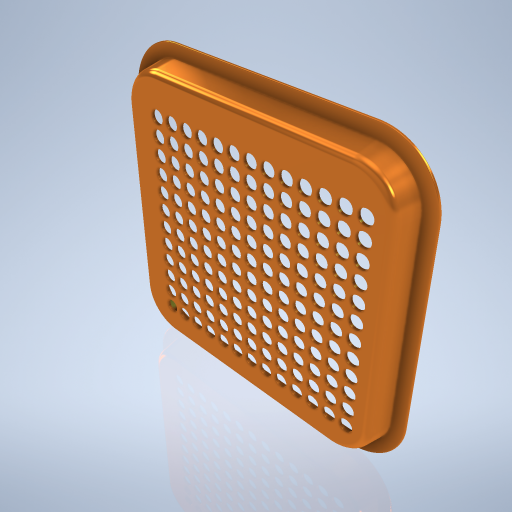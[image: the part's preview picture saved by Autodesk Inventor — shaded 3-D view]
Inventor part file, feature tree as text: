
AUTODESK INVENTOR PART (.ipt)
format: ipt  version: 2024.2 (Build 282272000, 272)  size: 988,672 bytes
history: native  units: mm
features: sketch x5, extrude x3, plane x2, mirror x2, fillet x2, pattern_linear x2, projected_geometry x2, revolve x1, other x1
ambient origin geometry x8: Origin, YZ Plane, XZ Plane, XY Plane, X Axis, Y Axis, Z Axis, Center Point
bodies: Body1 (feature_tree)
feature tree (20):
  extrude  "Extrusion4"  Depth=3.5mm
  revolve  "Umdrehung2"
  extrude  "Extrusion5"  Depth=3.5mm
  plane  "Arbeitsebene4"
  mirror  "Spiegeln4"
  plane  "Arbeitsebene5"
  mirror  "Spiegeln6"
  fillet  "Rundung1"  Radius=17.453293mm
  fillet  "Rundung2"  Radius=20.0mm
  extrude  "Extrusion6"  Depth=10.0mm
  pattern_linear  "Rechteckige Anordnung2"  Count1=12 Spacing1=0.0mm
  pattern_linear  "Rechteckige Anordnung3"  Count1=7  [1 undecoded]
  other  "Prägen1"
  sketch  "Skizze1"  dims[d0=195.0mm d1=3.5mm]
  sketch  "Skizze10"  dims[d2=3.5mm d3=3.5mm d4=17.453293mm d5=20.0mm]
  sketch  "Skizze11"  dims[d6=33.5mm d7=10.0mm d26=120.0mm d27=0.0mm d30=70.0mm]
  projected_geometry  "Projizierte Kontur5"
  sketch  "Skizze12"  dims[d31=90.0deg]
  projected_geometry  "Projizierte Kontur6"
  sketch  "Skizze13"  dims[d32=120.0mm d33=0.0mm d34=0.0mm d35=0.0mm d36=5.0mm d37=1.0mm d38=17.0mm d39=10.0mm d40=0.0mm d41=120.0mm d43=22.5mm d44=130.0mm d46=22.5mm d47=2.0mm d48=0.0mm d28=0.5mm d29=0.872665mm]
note: 1 required parameter value undecoded (feature->parameter linkage not recoverable at this tier; creation-order binding heuristic only, values carry confidence <= 0.55)
